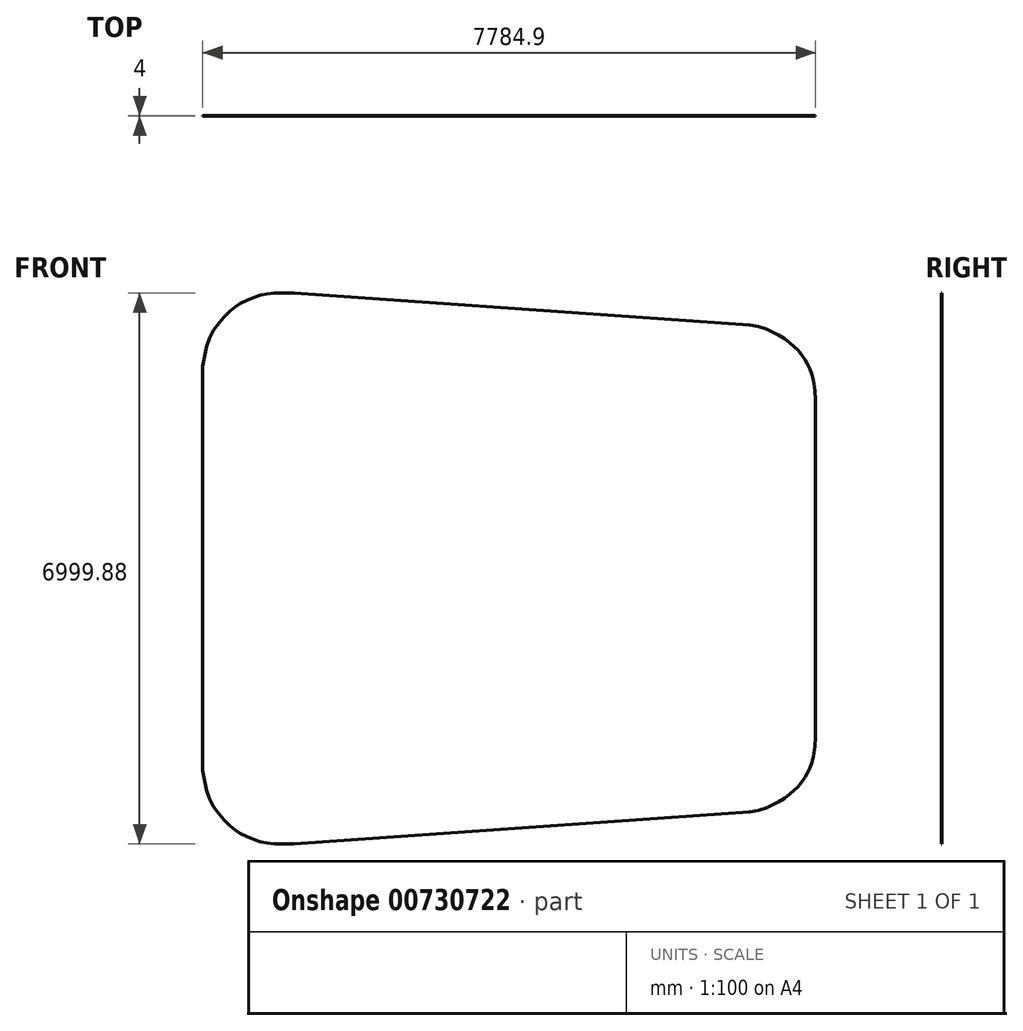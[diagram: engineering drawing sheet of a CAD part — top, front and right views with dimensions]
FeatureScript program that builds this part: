
annotation { "Feature Type Name" : "Feature", "Feature Type Description" : "" }
export const myFeature = defineFeature(function(context is Context, id is Id, definition is map)
    precondition{}
    {
        {
            var Q0;
            Q0=qCreatedBy(makeId("Front.planeOp"),FACE);
            var sketch = newSketch(context, id + "F0", { "sketchPlane" : qUnion([Q0])});
            skLineSegment(sketch, "E0", {"start": v(-3892.45, 1834.72) * mm, "end": v(-3765.45, 1834.72) * mm});
            skLineSegment(sketch, "E1", {"start": v(-3765.45, 1834.72) * mm, "end": v(-3892.45, 1834.72) * mm});
            skLineSegment(sketch, "E2", {"start": v(-3892.45, 1834.72) * mm, "end": v(-3891.71, 2566.14) * mm});
            skLineSegment(sketch, "E3", {"start": v(-3891.71, 2566.14) * mm, "end": v(-3764.71, 2566) * mm});
            skLineSegment(sketch, "E4", {"start": v(-3764.71, 2566) * mm, "end": v(-3891.71, 2566.14) * mm});
            skLineSegment(sketch, "E5", {"start": v(-3891.71, 2566.14) * mm, "end": v(-3872.76, 2692.76) * mm});
            skLineSegment(sketch, "E6", {"start": v(-3872.76, 2692.76) * mm, "end": v(-3844.06, 2817.93) * mm});
            skLineSegment(sketch, "E7", {"start": v(-3844.06, 2817.93) * mm, "end": v(-3807.92, 2929.71) * mm});
            skLineSegment(sketch, "E8", {"start": v(-3807.92, 2929.71) * mm, "end": v(-3754.8, 3026.08) * mm});
            skLineSegment(sketch, "E9", {"start": v(-3754.8, 3026.08) * mm, "end": v(-3688.51, 3115.39) * mm});
            skLineSegment(sketch, "E10", {"start": v(-3688.51, 3115.39) * mm, "end": v(-3619.98, 3196.49) * mm});
            skLineSegment(sketch, "E11", {"start": v(-3619.98, 3196.49) * mm, "end": v(-3545.13, 3270.86) * mm});
            skLineSegment(sketch, "E12", {"start": v(-3545.13, 3270.86) * mm, "end": v(-3483.08, 3320.26) * mm});
            skLineSegment(sketch, "E13", {"start": v(-3483.08, 3320.26) * mm, "end": v(-3416.45, 3363.54) * mm});
            skLineSegment(sketch, "E14", {"start": v(-3416.45, 3363.54) * mm, "end": v(-3323.26, 3411.04) * mm});
            skLineSegment(sketch, "E15", {"start": v(-3323.26, 3411.04) * mm, "end": v(-3225.7, 3449.42) * mm});
            skLineSegment(sketch, "E16", {"start": v(-3225.7, 3449.42) * mm, "end": v(-3155.8, 3471.42) * mm});
            skLineSegment(sketch, "E17", {"start": v(-3155.8, 3471.42) * mm, "end": v(-3084.58, 3487.52) * mm});
            skLineSegment(sketch, "E18", {"start": v(-3084.58, 3487.52) * mm, "end": v(-2989.07, 3497.58) * mm});
            skLineSegment(sketch, "E19", {"start": v(-2989.07, 3497.58) * mm, "end": v(-2892.63, 3499.94) * mm});
            skLineSegment(sketch, "E20", {"start": v(-2892.63, 3499.94) * mm, "end": v(-2730.42, 3497.94) * mm});
            skLineSegment(sketch, "E21", {"start": v(-2730.42, 3497.94) * mm, "end": v(-2732.02, 3370.94) * mm});
            skLineSegment(sketch, "E22", {"start": v(-2732.02, 3370.94) * mm, "end": v(-2730.42, 3497.94) * mm});
            skLineSegment(sketch, "E23", {"start": v(-2730.42, 3497.94) * mm, "end": v(3058.44, 3091.66) * mm});
            skLineSegment(sketch, "E24", {"start": v(3058.44, 3091.66) * mm, "end": v(3049.55, 2964.97) * mm});
            skLineSegment(sketch, "E25", {"start": v(3049.55, 2964.97) * mm, "end": v(3058.44, 3091.66) * mm});
            skLineSegment(sketch, "E26", {"start": v(3058.44, 3091.66) * mm, "end": v(3164.4, 3073.07) * mm});
            skLineSegment(sketch, "E27", {"start": v(3164.4, 3073.07) * mm, "end": v(3266.92, 3040.84) * mm});
            skLineSegment(sketch, "E28", {"start": v(3266.92, 3040.84) * mm, "end": v(3343.6, 3005.5) * mm});
            skLineSegment(sketch, "E29", {"start": v(3343.6, 3005.5) * mm, "end": v(3417.85, 2964.69) * mm});
            skLineSegment(sketch, "E30", {"start": v(3417.85, 2964.69) * mm, "end": v(3495.42, 2918.16) * mm});
            skLineSegment(sketch, "E31", {"start": v(3495.42, 2918.16) * mm, "end": v(3568.78, 2865.9) * mm});
            skLineSegment(sketch, "E32", {"start": v(3568.78, 2865.9) * mm, "end": v(3618.76, 2821.53) * mm});
            skLineSegment(sketch, "E33", {"start": v(3618.76, 2821.53) * mm, "end": v(3665.12, 2773.1) * mm});
            skLineSegment(sketch, "E34", {"start": v(3665.12, 2773.1) * mm, "end": v(3712.26, 2716.3) * mm});
            skLineSegment(sketch, "E35", {"start": v(3712.26, 2716.3) * mm, "end": v(3754.35, 2655.9) * mm});
            skLineSegment(sketch, "E36", {"start": v(3754.35, 2655.9) * mm, "end": v(3788.94, 2594.81) * mm});
            skLineSegment(sketch, "E37", {"start": v(3788.94, 2594.81) * mm, "end": v(3818.9, 2531.08) * mm});
            skLineSegment(sketch, "E38", {"start": v(3818.9, 2531.08) * mm, "end": v(3846.07, 2461.6) * mm});
            skLineSegment(sketch, "E39", {"start": v(3846.07, 2461.6) * mm, "end": v(3866.08, 2390.04) * mm});
            skLineSegment(sketch, "E40", {"start": v(3866.08, 2390.04) * mm, "end": v(3882.5, 2262.02) * mm});
            skLineSegment(sketch, "E41", {"start": v(3882.5, 2262.02) * mm, "end": v(3892.45, 2140.69) * mm});
            skLineSegment(sketch, "E42", {"start": v(3892.45, 2140.69) * mm, "end": v(3765.88, 2130.3) * mm});
            skLineSegment(sketch, "E43", {"start": v(3765.88, 2130.3) * mm, "end": v(3892.45, 2140.69) * mm});
            skLineSegment(sketch, "E44", {"start": v(3892.45, 2140.69) * mm, "end": v(3892.45, 1334.92) * mm});
            skLineSegment(sketch, "E45", {"start": v(3892.45, 1334.92) * mm, "end": v(3765.45, 1334.92) * mm});
            skLineSegment(sketch, "E46", {"start": v(3765.45, 1334.92) * mm, "end": v(3892.45, 1334.92) * mm});
            skLineSegment(sketch, "E47", {"start": v(3892.45, 1334.92) * mm, "end": v(3892.45, 844.45) * mm});
            skLineSegment(sketch, "E48", {"start": v(3892.45, 844.45) * mm, "end": v(3765.45, 844.45) * mm});
            skLineSegment(sketch, "E49", {"start": v(3765.45, 844.45) * mm, "end": v(3892.45, 844.45) * mm});
            skLineSegment(sketch, "E50", {"start": v(3892.45, 844.45) * mm, "end": v(3892.45, 0) * mm});
            skLineSegment(sketch, "E51", {"start": v(3892.45, 0) * mm, "end": v(3892.45, -844.42) * mm});
            skLineSegment(sketch, "E52", {"start": v(3892.45, -844.42) * mm, "end": v(3765.45, -844.42) * mm});
            skLineSegment(sketch, "E53", {"start": v(3765.45, -844.42) * mm, "end": v(3892.45, -844.42) * mm});
            skLineSegment(sketch, "E54", {"start": v(3892.45, -844.42) * mm, "end": v(3892.45, -1334.9) * mm});
            skLineSegment(sketch, "E55", {"start": v(3892.45, -1334.9) * mm, "end": v(3765.45, -1334.9) * mm});
            skLineSegment(sketch, "E56", {"start": v(3765.45, -1334.9) * mm, "end": v(3892.45, -1334.9) * mm});
            skLineSegment(sketch, "E57", {"start": v(3892.45, -1334.9) * mm, "end": v(3892.45, -2140.66) * mm});
            skLineSegment(sketch, "E58", {"start": v(3892.45, -2140.66) * mm, "end": v(3765.45, -2140.66) * mm});
            skLineSegment(sketch, "E59", {"start": v(3765.45, -2140.66) * mm, "end": v(3892.45, -2140.66) * mm});
            skLineSegment(sketch, "E60", {"start": v(3892.45, -2140.66) * mm, "end": v(3882.5, -2262) * mm});
            skLineSegment(sketch, "E61", {"start": v(3882.5, -2262) * mm, "end": v(3866.08, -2390.04) * mm});
            skLineSegment(sketch, "E62", {"start": v(3866.08, -2390.04) * mm, "end": v(3846.07, -2461.56) * mm});
            skLineSegment(sketch, "E63", {"start": v(3846.07, -2461.56) * mm, "end": v(3818.9, -2531.06) * mm});
            skLineSegment(sketch, "E64", {"start": v(3818.9, -2531.06) * mm, "end": v(3788.94, -2594.79) * mm});
            skLineSegment(sketch, "E65", {"start": v(3788.94, -2594.79) * mm, "end": v(3754.35, -2655.9) * mm});
            skLineSegment(sketch, "E66", {"start": v(3754.35, -2655.9) * mm, "end": v(3712.26, -2716.3) * mm});
            skLineSegment(sketch, "E67", {"start": v(3712.26, -2716.3) * mm, "end": v(3665.12, -2773.1) * mm});
            skLineSegment(sketch, "E68", {"start": v(3665.12, -2773.1) * mm, "end": v(3618.76, -2821.53) * mm});
            skLineSegment(sketch, "E69", {"start": v(3618.76, -2821.53) * mm, "end": v(3568.78, -2865.88) * mm});
            skLineSegment(sketch, "E70", {"start": v(3568.78, -2865.88) * mm, "end": v(3495.42, -2918.16) * mm});
            skLineSegment(sketch, "E71", {"start": v(3495.42, -2918.16) * mm, "end": v(3417.85, -2964.69) * mm});
            skLineSegment(sketch, "E72", {"start": v(3417.85, -2964.69) * mm, "end": v(3343.6, -3005.48) * mm});
            skLineSegment(sketch, "E73", {"start": v(3343.6, -3005.48) * mm, "end": v(3266.92, -3040.81) * mm});
            skLineSegment(sketch, "E74", {"start": v(3266.92, -3040.81) * mm, "end": v(3164.4, -3073.04) * mm});
            skLineSegment(sketch, "E75", {"start": v(3164.4, -3073.04) * mm, "end": v(3058.44, -3091.64) * mm});
            skLineSegment(sketch, "E76", {"start": v(3058.44, -3091.64) * mm, "end": v(3036.5, -2966.54) * mm});
            skLineSegment(sketch, "E77", {"start": v(3036.5, -2966.54) * mm, "end": v(3058.44, -3091.64) * mm});
            skLineSegment(sketch, "E78", {"start": v(3058.44, -3091.64) * mm, "end": v(-2730.42, -3497.91) * mm});
            skLineSegment(sketch, "E79", {"start": v(-2730.42, -3497.91) * mm, "end": v(-2739.31, -3371.22) * mm});
            skLineSegment(sketch, "E80", {"start": v(-2739.31, -3371.22) * mm, "end": v(-2730.42, -3497.91) * mm});
            skLineSegment(sketch, "E81", {"start": v(-2730.42, -3497.91) * mm, "end": v(-2892.63, -3499.94) * mm});
            skLineSegment(sketch, "E82", {"start": v(-2892.63, -3499.94) * mm, "end": v(-2989.07, -3497.58) * mm});
            skLineSegment(sketch, "E83", {"start": v(-2989.07, -3497.58) * mm, "end": v(-3084.58, -3487.52) * mm});
            skLineSegment(sketch, "E84", {"start": v(-3084.58, -3487.52) * mm, "end": v(-3155.8, -3471.42) * mm});
            skLineSegment(sketch, "E85", {"start": v(-3155.8, -3471.42) * mm, "end": v(-3225.7, -3449.4) * mm});
            skLineSegment(sketch, "E86", {"start": v(-3225.7, -3449.4) * mm, "end": v(-3323.26, -3411.04) * mm});
            skLineSegment(sketch, "E87", {"start": v(-3323.26, -3411.04) * mm, "end": v(-3416.45, -3363.52) * mm});
            skLineSegment(sketch, "E88", {"start": v(-3416.45, -3363.52) * mm, "end": v(-3483.08, -3320.26) * mm});
            skLineSegment(sketch, "E89", {"start": v(-3483.08, -3320.26) * mm, "end": v(-3545.13, -3270.83) * mm});
            skLineSegment(sketch, "E90", {"start": v(-3545.13, -3270.83) * mm, "end": v(-3619.98, -3196.46) * mm});
            skLineSegment(sketch, "E91", {"start": v(-3619.98, -3196.46) * mm, "end": v(-3688.51, -3115.36) * mm});
            skLineSegment(sketch, "E92", {"start": v(-3688.51, -3115.36) * mm, "end": v(-3754.8, -3026.05) * mm});
            skLineSegment(sketch, "E93", {"start": v(-3754.8, -3026.05) * mm, "end": v(-3807.92, -2929.71) * mm});
            skLineSegment(sketch, "E94", {"start": v(-3807.92, -2929.71) * mm, "end": v(-3844.06, -2817.9) * mm});
            skLineSegment(sketch, "E95", {"start": v(-3844.06, -2817.9) * mm, "end": v(-3872.76, -2692.76) * mm});
            skLineSegment(sketch, "E96", {"start": v(-3872.76, -2692.76) * mm, "end": v(-3891.71, -2566.11) * mm});
            skLineSegment(sketch, "E97", {"start": v(-3891.71, -2566.11) * mm, "end": v(-3766.1, -2547.32) * mm});
            skLineSegment(sketch, "E98", {"start": v(-3766.1, -2547.32) * mm, "end": v(-3891.71, -2566.11) * mm});
            skLineSegment(sketch, "E99", {"start": v(-3891.71, -2566.11) * mm, "end": v(-3892.45, -1834.72) * mm});
            skLineSegment(sketch, "E100", {"start": v(-3892.45, -1834.72) * mm, "end": v(-3765.45, -1834.6) * mm});
            skLineSegment(sketch, "E101", {"start": v(-3765.45, -1834.6) * mm, "end": v(-3892.45, -1834.72) * mm});
            skLineSegment(sketch, "E102", {"start": v(-3892.45, -1834.72) * mm, "end": v(-3892.45, -1334.9) * mm});
            skLineSegment(sketch, "E103", {"start": v(-3892.45, -1334.9) * mm, "end": v(-3765.45, -1334.9) * mm});
            skLineSegment(sketch, "E104", {"start": v(-3765.45, -1334.9) * mm, "end": v(-3892.45, -1334.9) * mm});
            skLineSegment(sketch, "E105", {"start": v(-3892.45, -1334.9) * mm, "end": v(-3892.45, 0) * mm});
            skLineSegment(sketch, "E106", {"start": v(-3892.45, 0) * mm, "end": v(-3892.45, 1334.92) * mm});
            skLineSegment(sketch, "E107", {"start": v(-3892.45, 1334.92) * mm, "end": v(-3765.45, 1334.92) * mm});
            skLineSegment(sketch, "E108", {"start": v(-3765.45, 1334.92) * mm, "end": v(-3892.45, 1334.92) * mm});
            skLineSegment(sketch, "E109", {"start": v(-3892.45, 1334.92) * mm, "end": v(-3892.45, 1834.72) * mm});
            skSolve(sketch);
        }
        {
            var Q0;
            Q0 = qSketchRegion(id + "F0", true);
            extrude(context, id + "F1", {"entities" : qUnion([Q0]), "depth" : 4 * mm, "offsetDistance" : 25 * mm});
        }
    });
